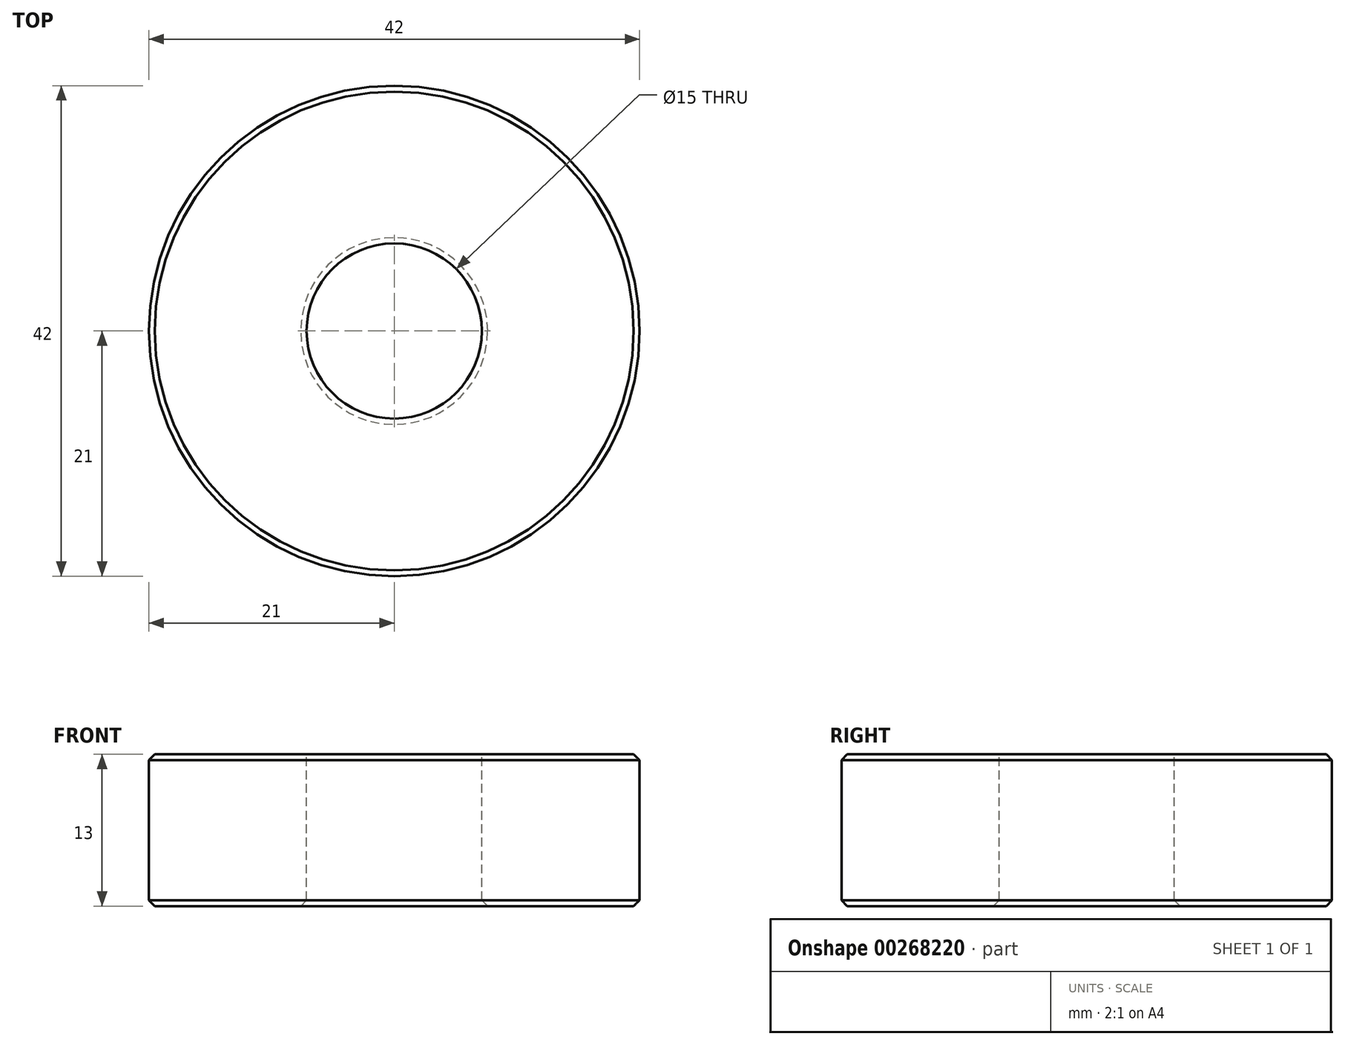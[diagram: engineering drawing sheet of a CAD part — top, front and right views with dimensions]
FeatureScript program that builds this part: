
annotation { "Feature Type Name" : "Feature", "Feature Type Description" : "" }
export const myFeature = defineFeature(function(context is Context, id is Id, definition is map)
    precondition{}
    {
        {
            var Q0;
            Q0=qCreatedBy(makeId("Top.planeOp"),FACE);
            var sketch = newSketch(context, id + "F0", { "sketchPlane" : qUnion([Q0])});
            skCircle(sketch, "E0", {"center": v(0, 0) * mm, "radius": 21 * mm});
            skSolve(sketch);
        }
        {
            var Q0;
            Q0 = qSketchRegion(id + "F0", true);
            extrude(context, id + "F1", {"entities" : qUnion([Q0]), "depth" : 13 * mm});
        }
        {
            var Q0;
            Q0=makeQuery(id+"F1.opExtrude","CAP_FACE",FACE,{"disambiguationData":[OSD([sQuery(id+"F0.wireOp",EDGE,"E0")])],"isStart":false});
            var sketch = newSketch(context, id + "F2", { "sketchPlane" : qUnion([Q0])});
            skCircle(sketch, "E1", {"center": v(0, 0) * mm, "radius": 7.5 * mm});
            skSolve(sketch);
        }
        {
            var Q0;
            Q0 = qSketchRegion(id + "F2", true);
            extrude(context, id + "F3", {"entities" : qUnion([Q0]), "operationType" : NewBodyOperationType.REMOVE, "oppositeDirection" : true, "depth" : 37.3 * mm});
        }
        {
            var Q0;
            Q0=makeQuery(id+"F1.opExtrude","CAP_EDGE",EDGE,{"disambiguationData":[OSD([sQuery(id+"F0.wireOp",EDGE,"E0")])],"isStart":false});
            var Q1;
            Q1=makeQuery(id+"F3.boolean.opBoolean","COPY",EDGE,{"derivedFrom":makeQuery(id+"F3.opExtrude","CAP_EDGE",EDGE,{"disambiguationData":[OSD([sQuery(id+"F2.wireOp",EDGE,"E1")])],"isStart":true})});
            var Q2;
            Q2=makeQuery(id+"F1.opExtrude","CAP_EDGE",EDGE,{"disambiguationData":[OSD([sQuery(id+"F0.wireOp",EDGE,"E0")])],"isStart":true});
            var Q3;
            Q3=makeQuery(id+"F3.boolean.opBoolean","INTERSECT",EDGE,{"derivedFrom":[makeQuery(id+"F1.opExtrude","CAP_FACE",FACE,{"disambiguationData":[OSD([sQuery(id+"F0.wireOp",EDGE,"E0")])],"isStart":true}),makeQuery(id+"F3.opExtrude","SWEPT_FACE",FACE,{"disambiguationData":[OSD([sQuery(id+"F2.wireOp",EDGE,"E1")])]})]});
            chamfer(context, id + "F4", {"entities" : qUnion([Q0, Q1, Q2, Q3]), "width" : 0.5 * mm, "tangentPropagation" : true});
        }
    });
